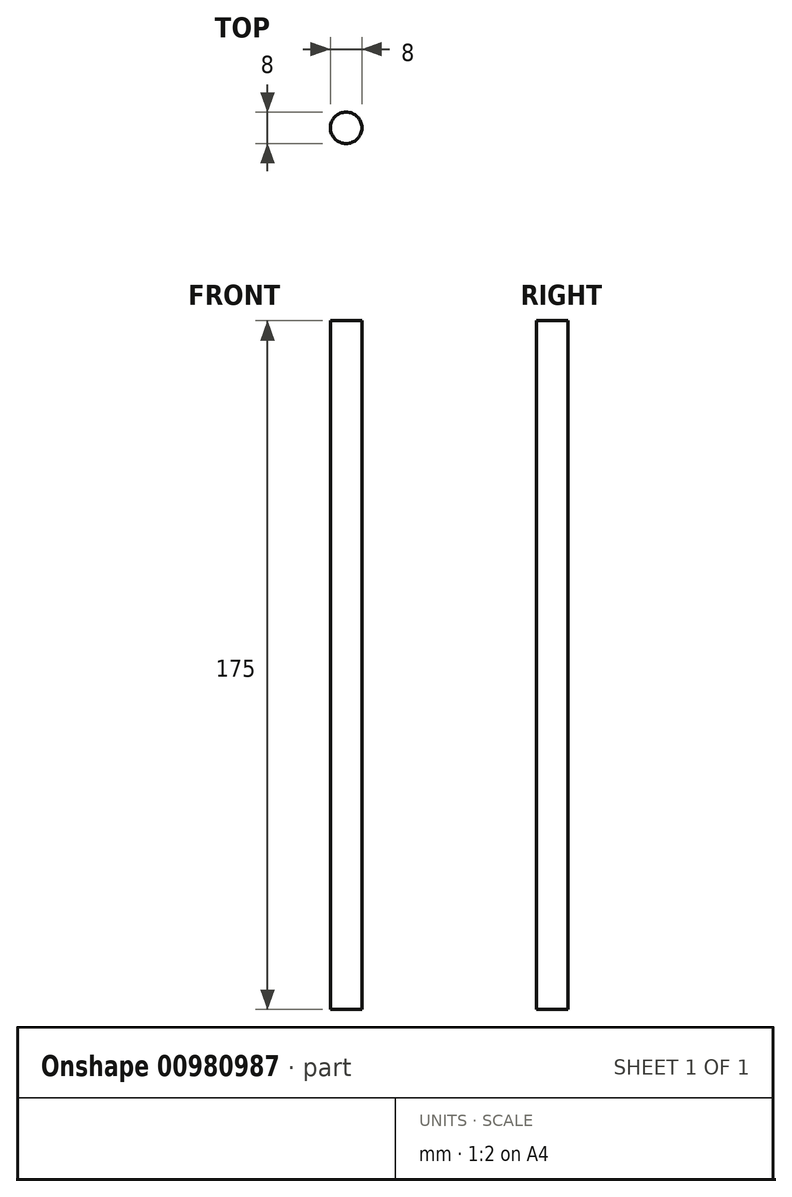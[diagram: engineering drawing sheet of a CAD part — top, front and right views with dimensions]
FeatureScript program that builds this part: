
annotation { "Feature Type Name" : "Feature", "Feature Type Description" : "" }
export const myFeature = defineFeature(function(context is Context, id is Id, definition is map)
    precondition{}
    {
        {
            var Q0;
            Q0=qCreatedBy(makeId("Top.planeOp"),FACE);
            var sketch = newSketch(context, id + "F0", { "sketchPlane" : qUnion([Q0])});
            skCircle(sketch, "E0", {"center": v(0, 0) * mm, "radius": 4 * mm});
            skSolve(sketch);
        }
        {
            var Q0;
            Q0=makeQuery(id+"F0.imprint","IMPRINT",FACE,{"disambiguationData":[TD([[makeQuery(id+"F0.imprint","IMPRINT",EDGE,{"derivedFrom":sQuery(id+"F0.wireOp",EDGE,"E0")}),1.0]])]});
            extrude(context, id + "F1", {"entities" : qUnion([Q0]), "depth" : 175 * mm, "offsetDistance" : 25 * mm});
        }
    });
